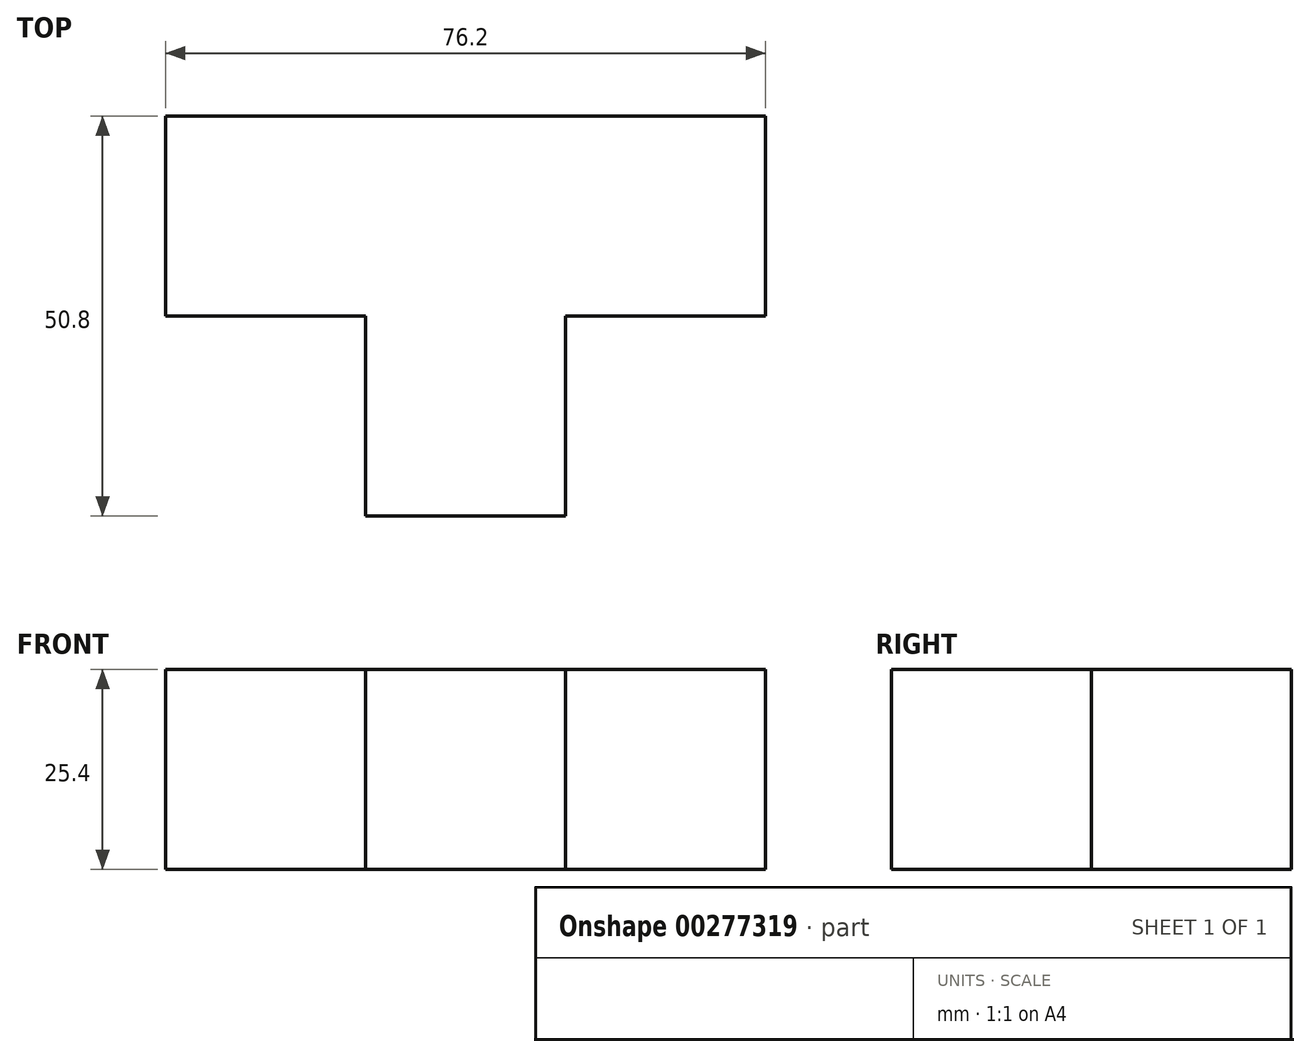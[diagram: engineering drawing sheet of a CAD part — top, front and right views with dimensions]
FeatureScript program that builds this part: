
annotation { "Feature Type Name" : "Feature", "Feature Type Description" : "" }
export const myFeature = defineFeature(function(context is Context, id is Id, definition is map)
    precondition{}
    {
        {
            var Q0;
            Q0=qCreatedBy(makeId("Front.planeOp"),FACE);
            var sketch = newSketch(context, id + "F0", { "sketchPlane" : qUnion([Q0])});
            skLineSegment(sketch, "E0", {"start": v(-48.5, -21.96) * mm, "end": v(-23.1, -21.96) * mm});
            skLineSegment(sketch, "E1", {"start": v(-23.1, -21.96) * mm, "end": v(2.3, -21.96) * mm});
            skLineSegment(sketch, "E2", {"start": v(2.3, -21.96) * mm, "end": v(27.7, -21.96) * mm});
            skLineSegment(sketch, "E3", {"start": v(27.7, -21.96) * mm, "end": v(27.7, 3.44) * mm});
            skLineSegment(sketch, "E4", {"start": v(27.7, 3.44) * mm, "end": v(2.3, 3.44) * mm});
            skLineSegment(sketch, "E5", {"start": v(2.3, 3.44) * mm, "end": v(-23.1, 3.44) * mm});
            skLineSegment(sketch, "E6", {"start": v(-23.1, 3.44) * mm, "end": v(-48.5, 3.44) * mm});
            skLineSegment(sketch, "E7", {"start": v(-48.5, 3.44) * mm, "end": v(-48.5, -21.96) * mm});
            skLineSegment(sketch, "E8", {"start": v(-23.1, -21.96) * mm, "end": v(-23.1, 3.44) * mm});
            skLineSegment(sketch, "E9", {"start": v(2.3, 3.44) * mm, "end": v(2.3, -21.96) * mm});
            skSolve(sketch);
        }
        {
            var Q0;
            Q0=makeQuery(id+"F0.imprint","IMPRINT",FACE,{"disambiguationData":[TD([[makeQuery(id+"F0.imprint","IMPRINT",EDGE,{"derivedFrom":sQuery(id+"F0.wireOp",EDGE,"E1")}),1.0]])]});
            extrude(context, id + "F1", {"entities" : qUnion([Q0]), "depth" : 50.8 * mm});
        }
        {
            var Q0;
            Q0=makeQuery(id+"F0.imprint","IMPRINT",FACE,{"disambiguationData":[TD([[makeQuery(id+"F0.imprint","IMPRINT",EDGE,{"derivedFrom":sQuery(id+"F0.wireOp",EDGE,"E0")}),1.0]])]});
            var Q1;
            Q1=makeQuery(id+"F0.imprint","IMPRINT",FACE,{"disambiguationData":[TD([[makeQuery(id+"F0.imprint","IMPRINT",EDGE,{"derivedFrom":sQuery(id+"F0.wireOp",EDGE,"E2")}),1.0]])]});
            extrude(context, id + "F2", {"entities" : qUnion([Q0, Q1]), "operationType" : NewBodyOperationType.ADD, "depth" : 25.4 * mm});
        }
    });
